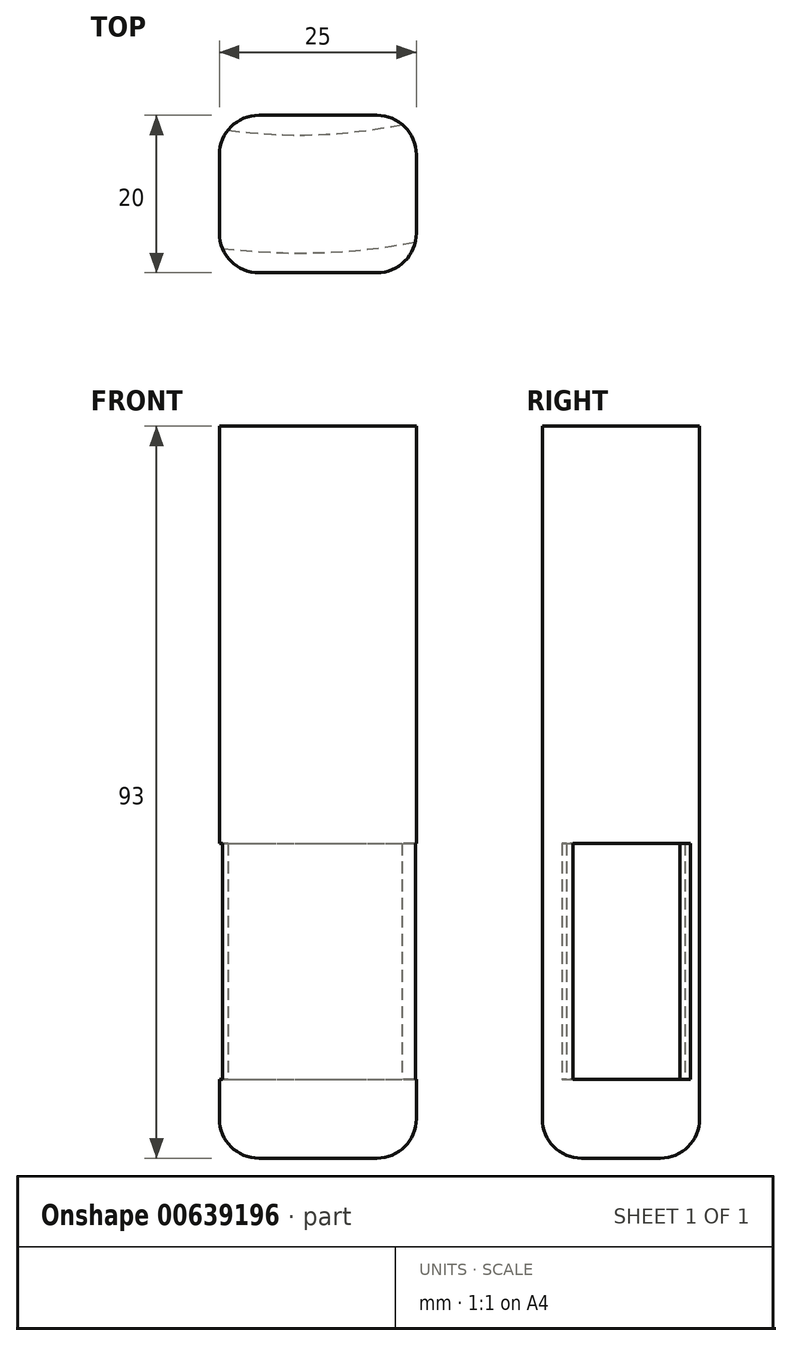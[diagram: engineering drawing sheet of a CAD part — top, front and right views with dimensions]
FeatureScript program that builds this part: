
annotation { "Feature Type Name" : "Feature", "Feature Type Description" : "" }
export const myFeature = defineFeature(function(context is Context, id is Id, definition is map)
    precondition{}
    {
        {
            var Q0;
            Q0=qCreatedBy(makeId("Top.planeOp"),FACE);
            var sketch = newSketch(context, id + "F0", { "sketchPlane" : qUnion([Q0])});
            skLineSegment(sketch, "E0.bottom", {"start": v(0, 10) * mm, "end": v(25, 10) * mm});
            skLineSegment(sketch, "E0.top", {"start": v(0, -10) * mm, "end": v(25, -10) * mm});
            skLineSegment(sketch, "E0.left", {"start": v(0, 10) * mm, "end": v(0, -10) * mm});
            skLineSegment(sketch, "E0.right", {"start": v(25, 10) * mm, "end": v(25, -10) * mm});
            skSolve(sketch);
        }
        {
            var Q0;
            Q0=makeQuery(id+"F0.imprint","IMPRINT",FACE,{"disambiguationData":[TD([[makeQuery(id+"F0.imprint","IMPRINT",EDGE,{"derivedFrom":sQuery(id+"F0.wireOp",EDGE,"E0.bottom")}),-1.0]])]});
            extrude(context, id + "F1", {"entities" : qUnion([Q0]), "depth" : 93 * mm, "offsetDistance" : 25 * mm});
        }
        {
            var Q0;
            Q0=qCreatedBy(makeId("Top.planeOp"),FACE);
            cPlane(context, id + "F2", {"entities" : qUnion([Q0]), "cplaneType" : CPlaneType.OFFSET, "offset" : 10 * mm, "width" : 150 * mm, "height" : 150 * mm});
        }
        {
            var Q0;
            Q0=qCreatedBy(id+"F2.planeOp",FACE);
            var sketch = newSketch(context, id + "F3", { "sketchPlane" : qUnion([Q0])});
            skCircle(sketch, "E1", {"center": v(10.07, 72.5) * mm, "radius": 65 * mm});
            skCircle(sketch, "E2.0", {"center": v(10.07, 72.5) * mm, "radius": 80 * mm});
            skLineSegment(sketch, "E3", {"start": v(10.07, 7.5) * mm, "end": v(10.07, -7.5) * mm, "construction": true});
            skPoint(sketch, "E4", {"position": v(10.07, 0) * mm});
            skSolve(sketch);
        }
        {
            var Q0;
            Q0=makeQuery(id+"F3.imprint","IMPRINT",FACE,{"disambiguationData":[TD([[makeQuery(id+"F3.imprint","IMPRINT",EDGE,{"derivedFrom":sQuery(id+"F3.wireOp",EDGE,"E1")}),-1.0]])]});
            extrude(context, id + "F4", {"entities" : qUnion([Q0]), "depth" : 30 * mm, "offsetDistance" : 25 * mm});
        }
        {
            var Q0;
            Q0=makeQuery(id+"F4.opExtrude","SWEPT_BODY",BODY,{"disambiguationData":[OSD([sQuery(id+"F3.wireOp",EDGE,"E1"),sQuery(id+"F3.wireOp",EDGE,"E2.0")])]});
            var Q1;
            Q1=makeQuery(id+"F1.opExtrude","SWEPT_BODY",BODY,{"disambiguationData":[OSD([sQuery(id+"F0.wireOp",EDGE,"E0.bottom"),sQuery(id+"F0.wireOp",EDGE,"E0.top"),sQuery(id+"F0.wireOp",EDGE,"E0.left"),sQuery(id+"F0.wireOp",EDGE,"E0.right")])]});
            booleanBodies(context, id + "F5", {"operationType" : BooleanOperationType.SUBTRACTION, "tools" : qUnion([Q0]), "targets" : qUnion([Q1])});
        }
        {
            var Q0;
            Q0=makeQuery(id+"F1.opExtrude","CAP_EDGE",EDGE,{"disambiguationData":[OSD([sQuery(id+"F0.wireOp",EDGE,"E0.left")])],"isStart":true});
            var Q1;
            Q1=makeQuery(id+"F1.opExtrude","CAP_EDGE",EDGE,{"disambiguationData":[OSD([sQuery(id+"F0.wireOp",EDGE,"E0.bottom")])],"isStart":true});
            var Q2;
            Q2=makeQuery(id+"F1.opExtrude","SWEPT_EDGE",EDGE,{"disambiguationData":[OSD([sQuery(id+"F0.wireOp",EDGE,"E0.top"),sQuery(id+"F0.wireOp",EDGE,"E0.right")])]});
            var Q3;
            Q3=makeQuery(id+"F1.opExtrude","CAP_EDGE",EDGE,{"disambiguationData":[OSD([sQuery(id+"F0.wireOp",EDGE,"E0.right")])],"isStart":true});
            var Q4;
            Q4=makeQuery(id+"F1.opExtrude","CAP_EDGE",EDGE,{"disambiguationData":[OSD([sQuery(id+"F0.wireOp",EDGE,"E0.top")])],"isStart":true});
            var Q5;
            Q5=makeQuery(id+"F1.opExtrude","SWEPT_EDGE",EDGE,{"disambiguationData":[OSD([sQuery(id+"F0.wireOp",EDGE,"E0.top"),sQuery(id+"F0.wireOp",EDGE,"E0.left")])]});
            var Q6;
            Q6=makeQuery(id+"F1.opExtrude","SWEPT_EDGE",EDGE,{"disambiguationData":[OSD([sQuery(id+"F0.wireOp",EDGE,"E0.bottom"),sQuery(id+"F0.wireOp",EDGE,"E0.left")])]});
            var Q7;
            Q7=makeQuery(id+"F1.opExtrude","SWEPT_EDGE",EDGE,{"disambiguationData":[OSD([sQuery(id+"F0.wireOp",EDGE,"E0.bottom"),sQuery(id+"F0.wireOp",EDGE,"E0.right")])]});
            fillet(context, id + "F6", {"entities" : qUnion([Q0, Q1, Q2, Q3, Q4, Q5, Q6, Q7]), "radius" : 5 * mm, "tangentPropagation" : true, "allowEdgeOverflow" : false});
        }
    });
